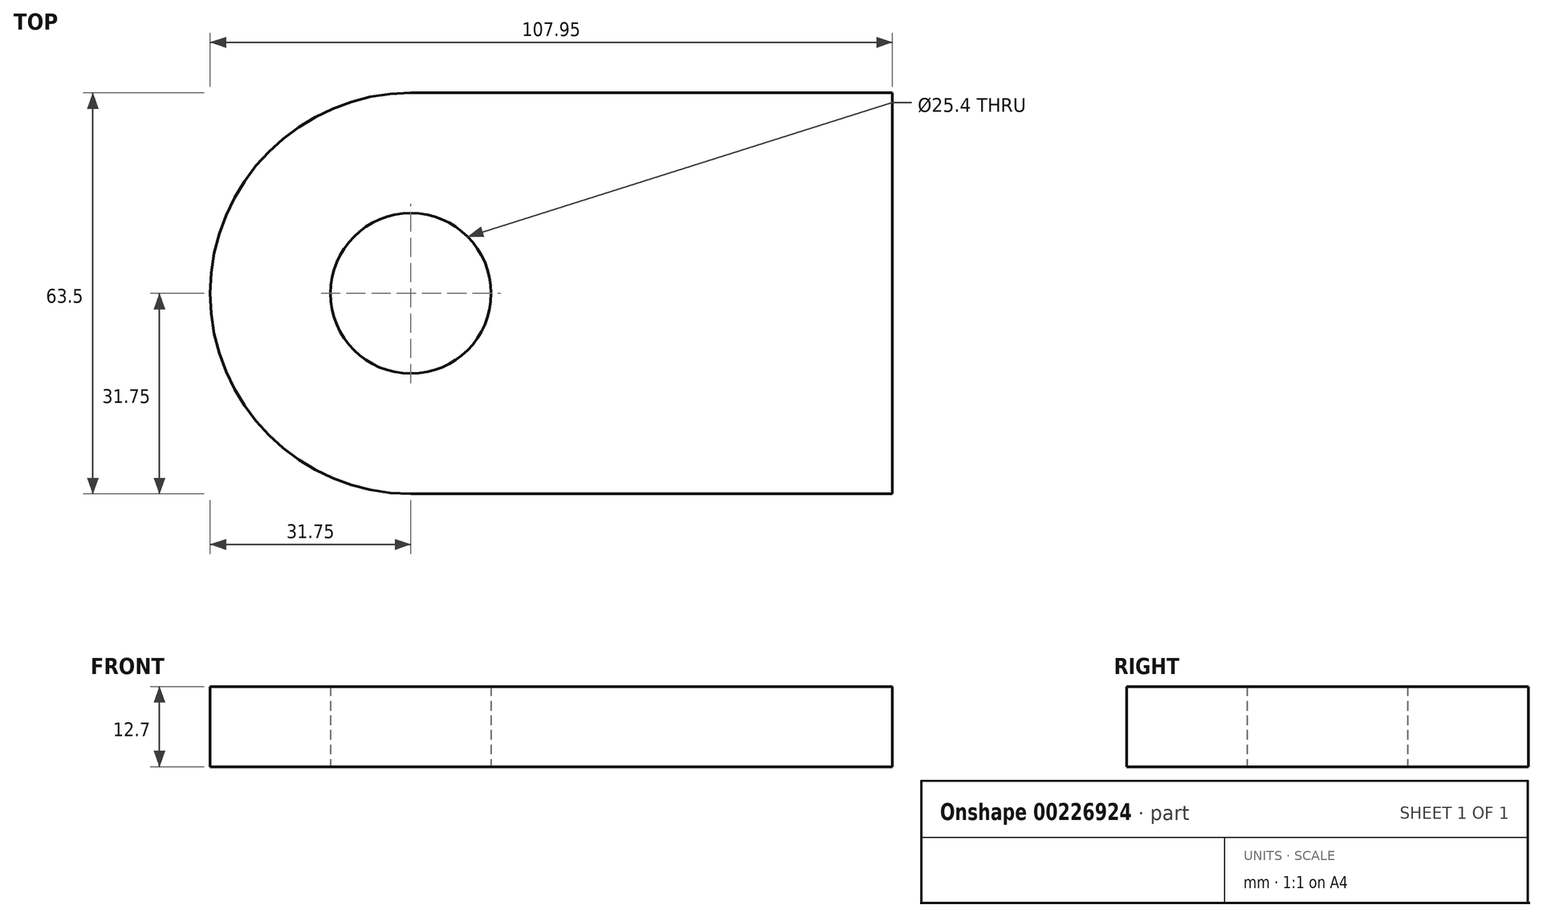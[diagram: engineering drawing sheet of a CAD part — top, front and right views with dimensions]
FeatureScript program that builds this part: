
annotation { "Feature Type Name" : "Feature", "Feature Type Description" : "" }
export const myFeature = defineFeature(function(context is Context, id is Id, definition is map)
    precondition{}
    {
        {
            var Q0;
            Q0=qCreatedBy(makeId("Top.planeOp"),FACE);
            var sketch = newSketch(context, id + "F0", { "sketchPlane" : qUnion([Q0])});
            skLineSegment(sketch, "E0.bottom", {"start": v(-38.1, 31.75) * mm, "end": v(38.1, 31.75) * mm});
            skLineSegment(sketch, "E0.top", {"start": v(-38.1, -31.75) * mm, "end": v(38.1, -31.75) * mm});
            skLineSegment(sketch, "E0.left", {"start": v(-38.1, 31.75) * mm, "end": v(-38.1, -31.75) * mm});
            skLineSegment(sketch, "E0.right", {"start": v(38.1, 31.75) * mm, "end": v(38.1, -31.75) * mm});
            skPoint(sketch, "E0.middle", {"position": v(0, 0) * mm});
            skCircle(sketch, "E1", {"center": v(-38.1, 0) * mm, "radius": 31.75 * mm});
            skCircle(sketch, "E2", {"center": v(-38.1, 0) * mm, "radius": 12.7 * mm});
            skSolve(sketch);
        }
        {
            var Q0;
            Q0 = qSketchRegion(id + "F0", true);
            extrude(context, id + "F1", {"entities" : qUnion([Q0]), "depth" : 12.7 * mm});
        }
    });
